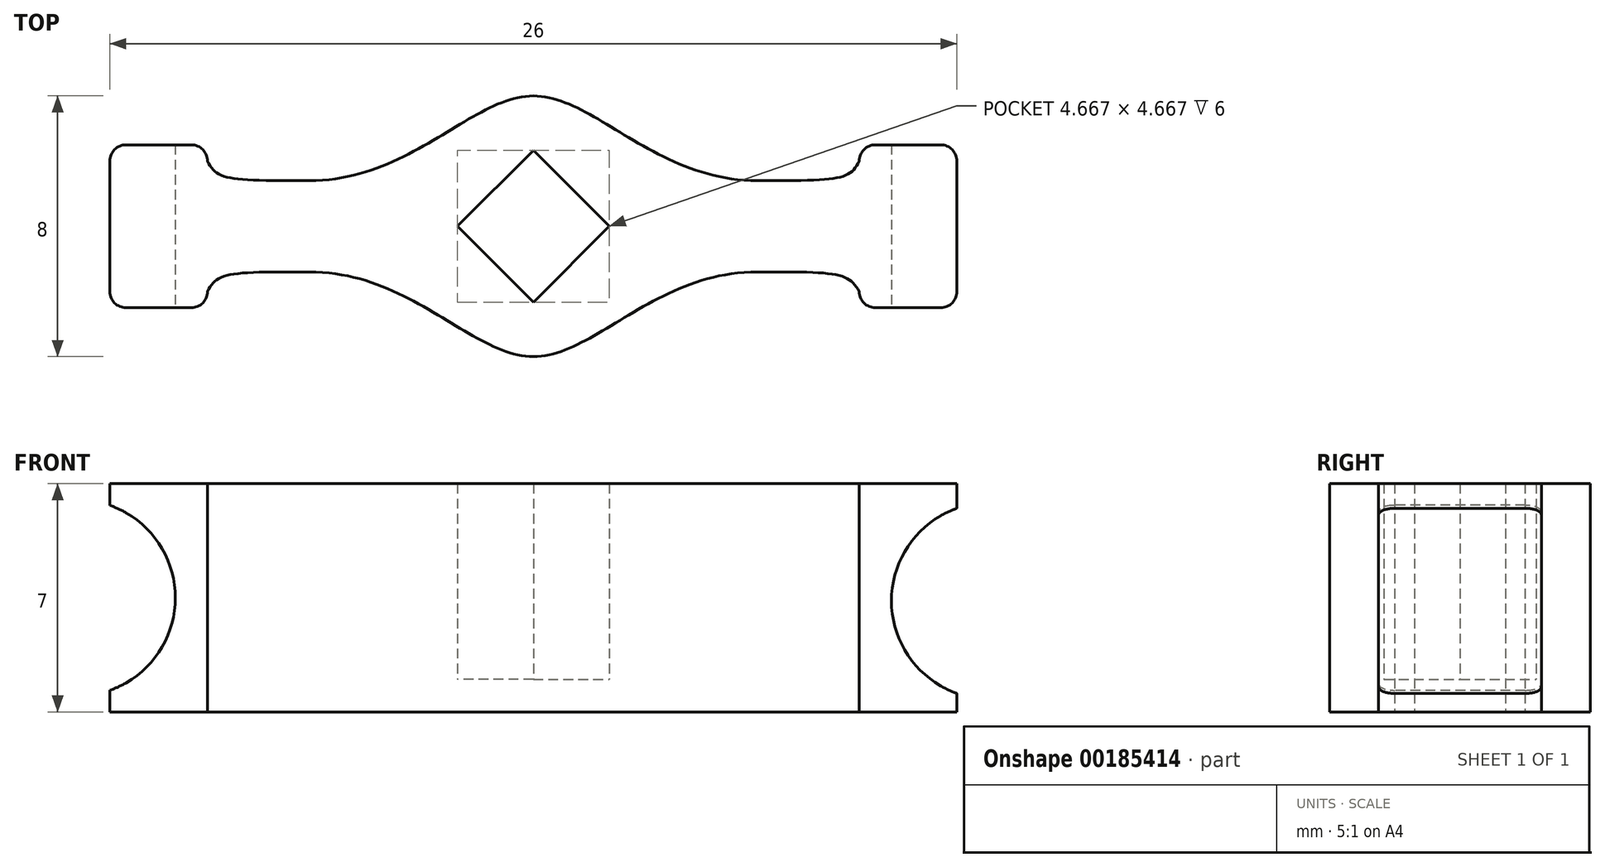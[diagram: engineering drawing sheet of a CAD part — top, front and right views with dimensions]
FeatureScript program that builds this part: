
annotation { "Feature Type Name" : "Feature", "Feature Type Description" : "" }
export const myFeature = defineFeature(function(context is Context, id is Id, definition is map)
    precondition{}
    {
        {
            var Q0;
            Q0=qCreatedBy(makeId("Top.planeOp"),FACE);
            var sketch = newSketch(context, id + "F0", { "sketchPlane" : qUnion([Q0])});
            skCircle(sketch, "E0", {"center": v(0, 0) * mm, "radius": 4 * mm});
            skLineSegment(sketch, "E1.bottom", {"start": v(12.5, 2.5) * mm, "end": v(10.5, 2.5) * mm});
            skLineSegment(sketch, "E1.top", {"start": v(12.5, -2.5) * mm, "end": v(10.5, -2.5) * mm});
            skLineSegment(sketch, "E1.left", {"start": v(13, 2) * mm, "end": v(13, -2) * mm});
            skLineSegment(sketch, "E1.right", {"start": v(10, 2) * mm, "end": v(10, -2) * mm});
            skPoint(sketch, "E1.middle", {"position": v(11.5, 0) * mm});
            skLineSegment(sketch, "E2.bottom", {"start": v(-10.5, 2.5) * mm, "end": v(-12.5, 2.5) * mm});
            skLineSegment(sketch, "E2.top", {"start": v(-10.5, -2.5) * mm, "end": v(-12.5, -2.5) * mm});
            skLineSegment(sketch, "E2.left", {"start": v(-10, 2) * mm, "end": v(-10, -2) * mm});
            skLineSegment(sketch, "E2.right", {"start": v(-13, 2) * mm, "end": v(-13, -2) * mm});
            skPoint(sketch, "E2.middle", {"position": v(-11.5, 0) * mm});
            skPoint(sketch, "E2.middle.positionSnap0", {"position": v(10, 0) * mm});
            skPoint(sketch, "E2.centerSnap0", {"position": v(10, 0) * mm});
            skLineSegment(sketch, "E3", {"start": v(0, 0) * mm, "end": v(-11.5, 0) * mm});
            skLineSegment(sketch, "E4", {"start": v(0, 0) * mm, "end": v(11.5, 0) * mm});
            skLineSegment(sketch, "E5", {"start": v(3.75, 1.4) * mm, "end": v(10, 1.4) * mm});
            skLineSegment(sketch, "E6", {"start": v(3.75, -1.4) * mm, "end": v(10, -1.4) * mm});
            skLineSegment(sketch, "E7", {"start": v(6.87, 1.4) * mm, "end": v(6.87, -1.4) * mm});
            skLineSegment(sketch, "E8", {"start": v(-3.75, 1.4) * mm, "end": v(-10, 1.4) * mm});
            skLineSegment(sketch, "E9", {"start": v(-3.75, -1.4) * mm, "end": v(-10, -1.4) * mm});
            skLineSegment(sketch, "E10", {"start": v(-6.87, 1.4) * mm, "end": v(-6.87, -1.4) * mm});
            skPoint(sketch, "E11.visualSharp", {"position": v(-10, 2.5) * mm});
            skArc(sketch, "E11.filletArc", {"start": v(-10, 2) * mm, "mid": v(-10.15, 2.35) * mm, "end": v(-10.5, 2.5) * mm});
            skPoint(sketch, "E12.visualSharp", {"position": v(-10, -2.5) * mm});
            skArc(sketch, "E12.filletArc", {"start": v(-10.5, -2.5) * mm, "mid": v(-10.15, -2.35) * mm, "end": v(-10, -2) * mm});
            skPoint(sketch, "E13.visualSharp", {"position": v(10, 2.5) * mm});
            skArc(sketch, "E13.filletArc", {"start": v(10.5, 2.5) * mm, "mid": v(10.15, 2.35) * mm, "end": v(10, 2) * mm});
            skPoint(sketch, "E14.visualSharp", {"position": v(10, -2.5) * mm});
            skArc(sketch, "E14.filletArc", {"start": v(10, -2) * mm, "mid": v(10.15, -2.35) * mm, "end": v(10.5, -2.5) * mm});
            skFitSpline(sketch, "E15", {"points": [v(-10, 2) * mm, v(-6.87, 1.4) * mm], "startDerivative": vector(0.89, -1.8) * mm, "endDerivative": vector(7.4, 0) * mm});
            skFitSpline(sketch, "E16", {"points": [v(-10, -2) * mm, v(-6.87, -1.4) * mm], "startDerivative": vector(0.89, 1.8) * mm, "endDerivative": vector(7.4, 0) * mm});
            skFitSpline(sketch, "E17", {"points": [v(6.87, 1.4) * mm, v(10, 2) * mm], "startDerivative": vector(7.42, 0) * mm, "endDerivative": vector(0.87, 1.8) * mm});
            skFitSpline(sketch, "E18", {"points": [v(6.87, -1.4) * mm, v(10, -2) * mm], "startDerivative": vector(7.3, 0) * mm, "endDerivative": vector(0.99, -1.8) * mm});
            skPoint(sketch, "E19.visualSharp", {"position": v(-13, 2.5) * mm});
            skArc(sketch, "E19.filletArc", {"start": v(-12.5, 2.5) * mm, "mid": v(-12.85, 2.35) * mm, "end": v(-13, 2) * mm});
            skPoint(sketch, "E20.visualSharp", {"position": v(-13, -2.5) * mm});
            skArc(sketch, "E20.filletArc", {"start": v(-13, -2) * mm, "mid": v(-12.85, -2.35) * mm, "end": v(-12.5, -2.5) * mm});
            skPoint(sketch, "E21.visualSharp", {"position": v(13, -2.5) * mm});
            skArc(sketch, "E21.filletArc", {"start": v(12.5, -2.5) * mm, "mid": v(12.85, -2.35) * mm, "end": v(13, -2) * mm});
            skPoint(sketch, "E22.visualSharp", {"position": v(13, 2.5) * mm});
            skArc(sketch, "E22.filletArc", {"start": v(13, 2) * mm, "mid": v(12.85, 2.35) * mm, "end": v(12.5, 2.5) * mm});
            skFitSpline(sketch, "E23", {"points": [v(-6.87, 1.4) * mm, v(0, 4) * mm, v(6.87, 1.4) * mm], "startDerivative": vector(18.76, 0) * mm, "endDerivative": vector(18.76, 0) * mm});
            skFitSpline(sketch, "E24", {"points": [v(-6.87, -1.4) * mm, v(0, -4) * mm, v(6.87, -1.4) * mm], "startDerivative": vector(18.76, 0) * mm, "endDerivative": vector(18.76, 0) * mm});
            skCircle(sketch, "E25.cCircle", {"center": v(0, 0) * mm, "radius": 2.33 * mm, "construction": true});
            skLineSegment(sketch, "E25.0", {"start": v(-2.33, 0) * mm, "end": v(0, 2.33) * mm});
            skLineSegment(sketch, "E25.1", {"start": v(0, 2.33) * mm, "end": v(2.33, 0) * mm});
            skLineSegment(sketch, "E25.2", {"start": v(2.33, 0) * mm, "end": v(0, -2.33) * mm});
            skLineSegment(sketch, "E25.3", {"start": v(0, -2.33) * mm, "end": v(-2.33, 0) * mm});
            skSolve(sketch);
        }
        {
            var Q0;
            Q0=makeQuery(id+"F0.imprint","IMPRINT",FACE,{"disambiguationData":[TD([[makeQuery(id+"F0.imprint","IMPRINT",EDGE,{"derivedFrom":sQuery(id+"F0.wireOp",EDGE,"E2.bottom")}),1.0]])]});
            var Q1;
            {var subQ0=sQuery(id+"F0.wireOp",EDGE,"E15");Q1=makeQuery(id+"F0.imprint","IMPRINT",FACE,{"disambiguationData":[TD([[makeQuery(id+"F0.imprint","IMPRINT",EDGE,{"derivedFrom":subQ0}),-1.0]])]});}
            var Q2;
            {var subQ0=sQuery(id+"F0.wireOp",EDGE,"E16");Q2=makeQuery(id+"F0.imprint","IMPRINT",FACE,{"disambiguationData":[TD([[makeQuery(id+"F0.imprint","IMPRINT",EDGE,{"derivedFrom":subQ0}),1.0]])]});}
            var Q3;
            {var subQ0=sQuery(id+"F0.wireOp",EDGE,"E8");var subQ1=sQuery(id+"F0.wireOp",EDGE,"E2.left");var subQ2=makeQuery(id+"F0.imprint","INTERSECT",VERTEX,{"derivedFrom":[subQ1,subQ0]});Q3=makeQuery(id+"F0.imprint","IMPRINT",FACE,{"disambiguationData":[TD([[makeQuery(id+"F0.imprint","IMPRINT",EDGE,{"disambiguationData":[TD([[subQ2,-1.0]])],"derivedFrom":subQ1}),1.0]])]});}
            var Q4;
            {var subQ0=sQuery(id+"F0.wireOp",EDGE,"E9");var subQ1=sQuery(id+"F0.wireOp",EDGE,"E2.left");var subQ2=makeQuery(id+"F0.imprint","INTERSECT",VERTEX,{"derivedFrom":[subQ1,subQ0]});Q4=makeQuery(id+"F0.imprint","IMPRINT",FACE,{"disambiguationData":[TD([[makeQuery(id+"F0.imprint","IMPRINT",EDGE,{"disambiguationData":[TD([[subQ2,1.0]])],"derivedFrom":subQ1}),1.0]])]});}
            var Q5;
            {var subQ0=sQuery(id+"F0.wireOp",EDGE,"E8");var subQ1=sQuery(id+"F0.wireOp",EDGE,"E0");var subQ2=makeQuery(id+"F0.imprint","INTERSECT",VERTEX,{"derivedFrom":[subQ1,subQ0]});Q5=makeQuery(id+"F0.imprint","IMPRINT",FACE,{"disambiguationData":[TD([[makeQuery(id+"F0.imprint","IMPRINT",EDGE,{"disambiguationData":[TD([[subQ2,-1.0]])],"derivedFrom":subQ1}),-1.0]])]});}
            var Q6;
            {var subQ0=sQuery(id+"F0.wireOp",EDGE,"E9");var subQ1=sQuery(id+"F0.wireOp",EDGE,"E0");var subQ2=makeQuery(id+"F0.imprint","INTERSECT",VERTEX,{"derivedFrom":[subQ1,subQ0]});Q6=makeQuery(id+"F0.imprint","IMPRINT",FACE,{"disambiguationData":[TD([[makeQuery(id+"F0.imprint","IMPRINT",EDGE,{"disambiguationData":[TD([[subQ2,1.0]])],"derivedFrom":subQ1}),-1.0]])]});}
            var Q7;
            {var subQ0=sQuery(id+"F0.wireOp",EDGE,"E8");var subQ1=sQuery(id+"F0.wireOp",EDGE,"E0");var subQ2=makeQuery(id+"F0.imprint","INTERSECT",VERTEX,{"derivedFrom":[subQ1,subQ0]});Q7=makeQuery(id+"F0.imprint","IMPRINT",FACE,{"disambiguationData":[TD([[makeQuery(id+"F0.imprint","IMPRINT",EDGE,{"disambiguationData":[TD([[subQ2,1.0]])],"derivedFrom":subQ1}),-1.0]])]});}
            var Q8;
            {var subQ0=sQuery(id+"F0.wireOp",EDGE,"E9");var subQ1=sQuery(id+"F0.wireOp",EDGE,"E0");var subQ2=makeQuery(id+"F0.imprint","INTERSECT",VERTEX,{"derivedFrom":[subQ1,subQ0]});Q8=makeQuery(id+"F0.imprint","IMPRINT",FACE,{"disambiguationData":[TD([[makeQuery(id+"F0.imprint","IMPRINT",EDGE,{"disambiguationData":[TD([[subQ2,-1.0]])],"derivedFrom":subQ1}),-1.0]])]});}
            var Q9;
            {var subQ0=sQuery(id+"F0.wireOp",EDGE,"E17");Q9=makeQuery(id+"F0.imprint","IMPRINT",FACE,{"disambiguationData":[TD([[makeQuery(id+"F0.imprint","IMPRINT",EDGE,{"derivedFrom":subQ0}),-1.0]])]});}
            var Q10;
            {var subQ0=sQuery(id+"F0.wireOp",EDGE,"E18");Q10=makeQuery(id+"F0.imprint","IMPRINT",FACE,{"disambiguationData":[TD([[makeQuery(id+"F0.imprint","IMPRINT",EDGE,{"derivedFrom":subQ0}),1.0]])]});}
            var Q11;
            {var subQ0=sQuery(id+"F0.wireOp",EDGE,"E5");var subQ1=sQuery(id+"F0.wireOp",EDGE,"E1.right");var subQ2=makeQuery(id+"F0.imprint","INTERSECT",VERTEX,{"derivedFrom":[subQ1,subQ0]});Q11=makeQuery(id+"F0.imprint","IMPRINT",FACE,{"disambiguationData":[TD([[makeQuery(id+"F0.imprint","IMPRINT",EDGE,{"disambiguationData":[TD([[subQ2,-1.0]])],"derivedFrom":subQ1}),-1.0]])]});}
            var Q12;
            {var subQ0=sQuery(id+"F0.wireOp",EDGE,"E6");var subQ1=sQuery(id+"F0.wireOp",EDGE,"E1.right");var subQ2=makeQuery(id+"F0.imprint","INTERSECT",VERTEX,{"derivedFrom":[subQ1,subQ0]});Q12=makeQuery(id+"F0.imprint","IMPRINT",FACE,{"disambiguationData":[TD([[makeQuery(id+"F0.imprint","IMPRINT",EDGE,{"disambiguationData":[TD([[subQ2,1.0]])],"derivedFrom":subQ1}),-1.0]])]});}
            var Q13;
            {var subQ0=sQuery(id+"F0.wireOp",EDGE,"E5");var subQ1=sQuery(id+"F0.wireOp",EDGE,"E0");var subQ2=makeQuery(id+"F0.imprint","INTERSECT",VERTEX,{"derivedFrom":[subQ1,subQ0]});Q13=makeQuery(id+"F0.imprint","IMPRINT",FACE,{"disambiguationData":[TD([[makeQuery(id+"F0.imprint","IMPRINT",EDGE,{"disambiguationData":[TD([[subQ2,1.0]])],"derivedFrom":subQ1}),-1.0]])]});}
            var Q14;
            {var subQ0=sQuery(id+"F0.wireOp",EDGE,"E6");var subQ1=sQuery(id+"F0.wireOp",EDGE,"E0");var subQ2=makeQuery(id+"F0.imprint","INTERSECT",VERTEX,{"derivedFrom":[subQ1,subQ0]});Q14=makeQuery(id+"F0.imprint","IMPRINT",FACE,{"disambiguationData":[TD([[makeQuery(id+"F0.imprint","IMPRINT",EDGE,{"disambiguationData":[TD([[subQ2,-1.0]])],"derivedFrom":subQ1}),-1.0]])]});}
            var Q15;
            {var subQ0=sQuery(id+"F0.wireOp",EDGE,"E5");var subQ1=sQuery(id+"F0.wireOp",EDGE,"E0");var subQ2=makeQuery(id+"F0.imprint","INTERSECT",VERTEX,{"derivedFrom":[subQ1,subQ0]});Q15=makeQuery(id+"F0.imprint","IMPRINT",FACE,{"disambiguationData":[TD([[makeQuery(id+"F0.imprint","IMPRINT",EDGE,{"disambiguationData":[TD([[subQ2,-1.0]])],"derivedFrom":subQ1}),-1.0]])]});}
            var Q16;
            {var subQ0=sQuery(id+"F0.wireOp",EDGE,"E6");var subQ1=sQuery(id+"F0.wireOp",EDGE,"E0");var subQ2=makeQuery(id+"F0.imprint","INTERSECT",VERTEX,{"derivedFrom":[subQ1,subQ0]});Q16=makeQuery(id+"F0.imprint","IMPRINT",FACE,{"disambiguationData":[TD([[makeQuery(id+"F0.imprint","IMPRINT",EDGE,{"disambiguationData":[TD([[subQ2,1.0]])],"derivedFrom":subQ1}),-1.0]])]});}
            var Q17;
            {var subQ7=sQuery(id+"F0.wireOp",EDGE,"E25.0");Q17=makeQuery(id+"F0.imprint","IMPRINT",FACE,{"disambiguationData":[TD([[makeQuery(id+"F0.imprint","IMPRINT",EDGE,{"derivedFrom":subQ7}),1.0]])]});}
            var Q18;
            {var subQ11=sQuery(id+"F0.wireOp",EDGE,"E25.2");Q18=makeQuery(id+"F0.imprint","IMPRINT",FACE,{"disambiguationData":[TD([[makeQuery(id+"F0.imprint","IMPRINT",EDGE,{"derivedFrom":subQ11}),1.0]])]});}
            var Q19;
            {var subQ4=sQuery(id+"F0.wireOp",EDGE,"E25.2");Q19=makeQuery(id+"F0.imprint","IMPRINT",FACE,{"disambiguationData":[TD([[makeQuery(id+"F0.imprint","IMPRINT",EDGE,{"derivedFrom":subQ4}),-1.0]])]});}
            var Q20;
            {var subQ3=sQuery(id+"F0.wireOp",EDGE,"E25.0");Q20=makeQuery(id+"F0.imprint","IMPRINT",FACE,{"disambiguationData":[TD([[makeQuery(id+"F0.imprint","IMPRINT",EDGE,{"derivedFrom":subQ3}),-1.0]])]});}
            var Q21;
            Q21=makeQuery(id+"F0.imprint","IMPRINT",FACE,{"disambiguationData":[TD([[makeQuery(id+"F0.imprint","IMPRINT",EDGE,{"derivedFrom":sQuery(id+"F0.wireOp",EDGE,"E1.bottom")}),1.0]])]});
            extrude(context, id + "F1", {"entities" : qUnion([Q0, Q1, Q2, Q3, Q4, Q5, Q6, Q7, Q8, Q9, Q10, Q11, Q12, Q13, Q14, Q15, Q16, Q17, Q18, Q19, Q20, Q21]), "depth" : 1 * mm});
        }
        {
            var Q0;
            Q0=makeQuery(id+"F1.opExtrude","CAP_FACE",FACE,{"disambiguationData":[OSD([sQuery(id+"F0.wireOp",EDGE,"E1.bottom"),sQuery(id+"F0.wireOp",EDGE,"E1.top"),sQuery(id+"F0.wireOp",EDGE,"E1.left"),sQuery(id+"F0.wireOp",EDGE,"E2.bottom"),sQuery(id+"F0.wireOp",EDGE,"E2.top"),sQuery(id+"F0.wireOp",EDGE,"E2.right"),sQuery(id+"F0.wireOp",EDGE,"E11.filletArc"),sQuery(id+"F0.wireOp",EDGE,"E12.filletArc"),sQuery(id+"F0.wireOp",EDGE,"E13.filletArc"),sQuery(id+"F0.wireOp",EDGE,"E14.filletArc"),sQuery(id+"F0.wireOp",EDGE,"E15"),sQuery(id+"F0.wireOp",EDGE,"E16"),sQuery(id+"F0.wireOp",EDGE,"E17"),sQuery(id+"F0.wireOp",EDGE,"E18"),sQuery(id+"F0.wireOp",EDGE,"E19.filletArc"),sQuery(id+"F0.wireOp",EDGE,"E20.filletArc"),sQuery(id+"F0.wireOp",EDGE,"E21.filletArc"),sQuery(id+"F0.wireOp",EDGE,"E22.filletArc"),sQuery(id+"F0.wireOp",EDGE,"E23"),sQuery(id+"F0.wireOp",EDGE,"E24")])],"isStart":false});
            var sketch = newSketch(context, id + "F2", { "sketchPlane" : qUnion([Q0])});
            skCircle(sketch, "E26.cCircle", {"center": v(0, 0) * mm, "radius": 2.33 * mm, "construction": true});
            skLineSegment(sketch, "E26.0", {"start": v(-2.33, 0) * mm, "end": v(0, 2.33) * mm});
            skLineSegment(sketch, "E26.1", {"start": v(0, 2.33) * mm, "end": v(2.33, 0) * mm});
            skLineSegment(sketch, "E26.2", {"start": v(2.33, 0) * mm, "end": v(0, -2.33) * mm});
            skLineSegment(sketch, "E26.3", {"start": v(0, -2.33) * mm, "end": v(-2.33, 0) * mm});
            skSolve(sketch);
        }
        {
            var Q0;
            Q0=makeQuery(id+"F2.imprint","IMPRINT",FACE,{"disambiguationData":[TD([[makeQuery(id+"F2.imprint","IMPRINT",EDGE,{"derivedFrom":sQuery(id+"F2.wireOp",EDGE,"E26.0")}),1.0]])]});
            extrude(context, id + "F3", {"entities" : qUnion([Q0]), "operationType" : NewBodyOperationType.ADD, "depth" : 6 * mm});
        }
        {
            var Q0;
            Q0=qCreatedBy(makeId("Front.planeOp"),FACE);
            var sketch = newSketch(context, id + "F4", { "sketchPlane" : qUnion([Q0])});
            skLineSegment(sketch, "E27", {"start": v(-14, 3.5) * mm, "end": v(0, 3.5) * mm});
            skLineSegment(sketch, "E28", {"start": v(0, 3.5) * mm, "end": v(14, 3.4) * mm});
            skCircle(sketch, "E29", {"center": v(-14, 3.5) * mm, "radius": 3 * mm});
            skCircle(sketch, "E30", {"center": v(14, 3.4) * mm, "radius": 3 * mm});
            skSolve(sketch);
        }
        {
            var Q0;
            Q0=makeQuery(id+"F4.imprint","IMPRINT",FACE,{"disambiguationData":[TD([[makeQuery(id+"F4.imprint","IMPRINT",EDGE,{"derivedFrom":sQuery(id+"F4.wireOp",EDGE,"E29")}),1.0]])]});
            var Q1;
            Q1=makeQuery(id+"F4.imprint","IMPRINT",FACE,{"disambiguationData":[TD([[makeQuery(id+"F4.imprint","IMPRINT",EDGE,{"derivedFrom":sQuery(id+"F4.wireOp",EDGE,"E30")}),1.0]])]});
            extrude(context, id + "F5", {"entities" : qUnion([Q0, Q1]), "operationType" : NewBodyOperationType.REMOVE, "endBound" : BoundingType.SYMMETRIC, "oppositeDirection" : true, "depth" : 5 * mm});
        }
    });
